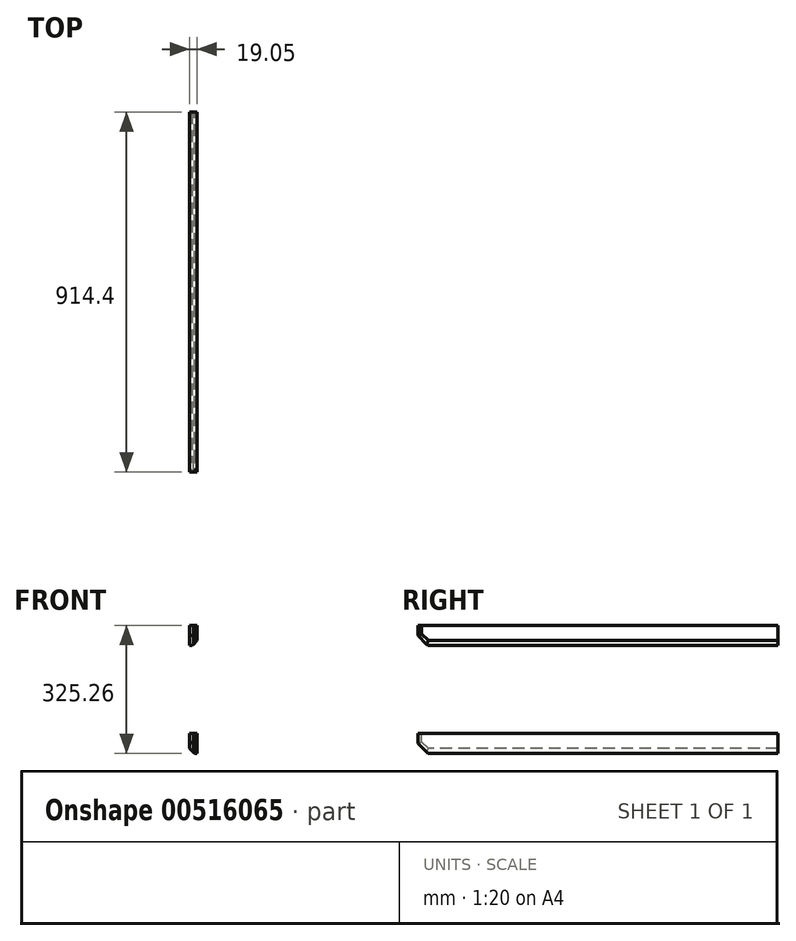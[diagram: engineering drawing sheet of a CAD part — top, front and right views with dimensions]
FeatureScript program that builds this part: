
annotation { "Feature Type Name" : "Feature", "Feature Type Description" : "" }
export const myFeature = defineFeature(function(context is Context, id is Id, definition is map)
    precondition{}
    {
        {
            var Q0;
            Q0=qCreatedBy(makeId("Right.planeOp"),FACE);
            var sketch = newSketch(context, id + "F0", { "sketchPlane" : qUnion([Q0])});
            skLineSegment(sketch, "E0.bottom", {"start": v(457.2, -25.4) * mm, "end": v(-457.2, -25.4) * mm});
            skLineSegment(sketch, "E0.top", {"start": v(457.2, 25.4) * mm, "end": v(-457.2, 25.4) * mm});
            skLineSegment(sketch, "E0.left", {"start": v(457.2, -25.4) * mm, "end": v(457.2, 25.4) * mm});
            skLineSegment(sketch, "E0.right", {"start": v(-457.2, -25.4) * mm, "end": v(-457.2, 25.4) * mm});
            skPoint(sketch, "E0.middle", {"position": v(0, 0) * mm});
            skLineSegment(sketch, "E1", {"start": v(-506.15, -137.23) * mm, "end": v(470.5, -137.23) * mm, "construction": true});
            skPoint(sketch, "E2.MirrorP", {"position": v(0, -274.46) * mm});
            skLineSegment(sketch, "E3.MirrorCS", {"start": v(457.2, -249.06) * mm, "end": v(-457.2, -249.06) * mm});
            skLineSegment(sketch, "E4.MirrorCS", {"start": v(457.2, -299.86) * mm, "end": v(-457.2, -299.86) * mm});
            skLineSegment(sketch, "E5.MirrorCS", {"start": v(457.2, -249.06) * mm, "end": v(457.2, -299.86) * mm});
            skLineSegment(sketch, "E6.MirrorCS", {"start": v(-457.2, -249.06) * mm, "end": v(-457.2, -299.86) * mm});
            skSolve(sketch);
        }
        {
            var Q0;
            Q0=makeQuery(id+"F0.imprint","IMPRINT",FACE,{"disambiguationData":[TD([[makeQuery(id+"F0.imprint","IMPRINT",EDGE,{"derivedFrom":sQuery(id+"F0.wireOp",EDGE,"E0.bottom")}),-1.0]])]});
            extrude(context, id + "F1", {"entities" : qUnion([Q0]), "depth" : 19.05 * mm, "offsetDistance" : 25.4 * mm});
        }
        {
            var Q0;
            Q0=makeQuery(id+"F1.opExtrude","SWEPT_EDGE",EDGE,{"disambiguationData":[OSD([sQuery(id+"F0.wireOp",EDGE,"E0.bottom"),sQuery(id+"F0.wireOp",EDGE,"E0.right")])]});
            chamfer(context, id + "F2", {"entities" : qUnion([Q0]), "width" : 25.4 * mm, "tangentPropagation" : true});
        }
        {
            var Q0;
            Q0=makeQuery(id+"F1.opExtrude","CAP_EDGE",EDGE,{"disambiguationData":[OSD([sQuery(id+"F0.wireOp",EDGE,"E0.bottom")])],"isStart":false});
            chamfer(context, id + "F3", {"entities" : qUnion([Q0]), "width" : 12.7 * mm, "tangentPropagation" : true});
        }
        {
            var Q0;
            Q0=makeQuery(id+"F0.imprint","IMPRINT",FACE,{"disambiguationData":[TD([[makeQuery(id+"F0.imprint","IMPRINT",EDGE,{"derivedFrom":sQuery(id+"F0.wireOp",EDGE,"E3.MirrorCS")}),1.0]])]});
            extrude(context, id + "F4", {"entities" : qUnion([Q0]), "depth" : 19.05 * mm, "offsetDistance" : 25.4 * mm});
        }
        {
            var Q0;
            Q0=makeQuery(id+"F4.opExtrude","SWEPT_EDGE",EDGE,{"disambiguationData":[OSD([sQuery(id+"F0.wireOp",EDGE,"E4.MirrorCS"),sQuery(id+"F0.wireOp",EDGE,"E6.MirrorCS")])]});
            chamfer(context, id + "F5", {"entities" : qUnion([Q0]), "width" : 25.4 * mm, "tangentPropagation" : true});
        }
        {
            var Q0;
            Q0=makeQuery(id+"F4.opExtrude","CAP_EDGE",EDGE,{"disambiguationData":[OSD([sQuery(id+"F0.wireOp",EDGE,"E4.MirrorCS")])],"isStart":true});
            chamfer(context, id + "F6", {"entities" : qUnion([Q0]), "width" : 12.7 * mm, "tangentPropagation" : true});
        }
        {
            var Q0;
            Q0=makeQuery(id+"F1.opExtrude","CAP_EDGE",EDGE,{"disambiguationData":[OSD([sQuery(id+"F0.wireOp",EDGE,"E0.right")])],"isStart":false});
            var Q1;
            {var subQ0=sQuery(id+"F0.wireOp",EDGE,"E0.right");var subQ1=sQuery(id+"F0.wireOp",EDGE,"E0.bottom");Q1=makeQuery(id+"F2.opChamfer","BLEND_EDGE",EDGE,{"blendedFrom":[makeQuery(id+"F1.opExtrude","SWEPT_EDGE",EDGE,{"disambiguationData":[OSD([subQ1,subQ0])]}),makeQuery(id+"F1.opExtrude","CAP_FACE",FACE,{"disambiguationData":[OSD([subQ1,sQuery(id+"F0.wireOp",EDGE,"E0.top"),sQuery(id+"F0.wireOp",EDGE,"E0.left"),subQ0])],"isStart":false})],"blendedInto":[makeQuery(id+"F1.opExtrude","CAP_FACE",FACE,{"disambiguationData":[OSD([subQ1,sQuery(id+"F0.wireOp",EDGE,"E0.top"),sQuery(id+"F0.wireOp",EDGE,"E0.left"),subQ0])],"isStart":false})]});}
            var Q2;
            {var subQ0=sQuery(id+"F0.wireOp",EDGE,"E6.MirrorCS");var subQ1=sQuery(id+"F0.wireOp",EDGE,"E4.MirrorCS");Q2=makeQuery(id+"F5.opChamfer","BLEND_EDGE",EDGE,{"blendedFrom":[makeQuery(id+"F4.opExtrude","SWEPT_EDGE",EDGE,{"disambiguationData":[OSD([subQ1,subQ0])]}),makeQuery(id+"F4.opExtrude","CAP_FACE",FACE,{"disambiguationData":[OSD([sQuery(id+"F0.wireOp",EDGE,"E3.MirrorCS"),subQ1,sQuery(id+"F0.wireOp",EDGE,"E5.MirrorCS"),subQ0])],"isStart":true})],"blendedInto":[makeQuery(id+"F4.opExtrude","CAP_FACE",FACE,{"disambiguationData":[OSD([sQuery(id+"F0.wireOp",EDGE,"E3.MirrorCS"),subQ1,sQuery(id+"F0.wireOp",EDGE,"E5.MirrorCS"),subQ0])],"isStart":true})]});}
            var Q3;
            Q3=makeQuery(id+"F4.opExtrude","CAP_EDGE",EDGE,{"disambiguationData":[OSD([sQuery(id+"F0.wireOp",EDGE,"E6.MirrorCS")])],"isStart":true});
            chamfer(context, id + "F7", {"entities" : qUnion([Q0, Q1, Q2, Q3]), "width" : 9.52 * mm, "tangentPropagation" : true});
        }
    });
